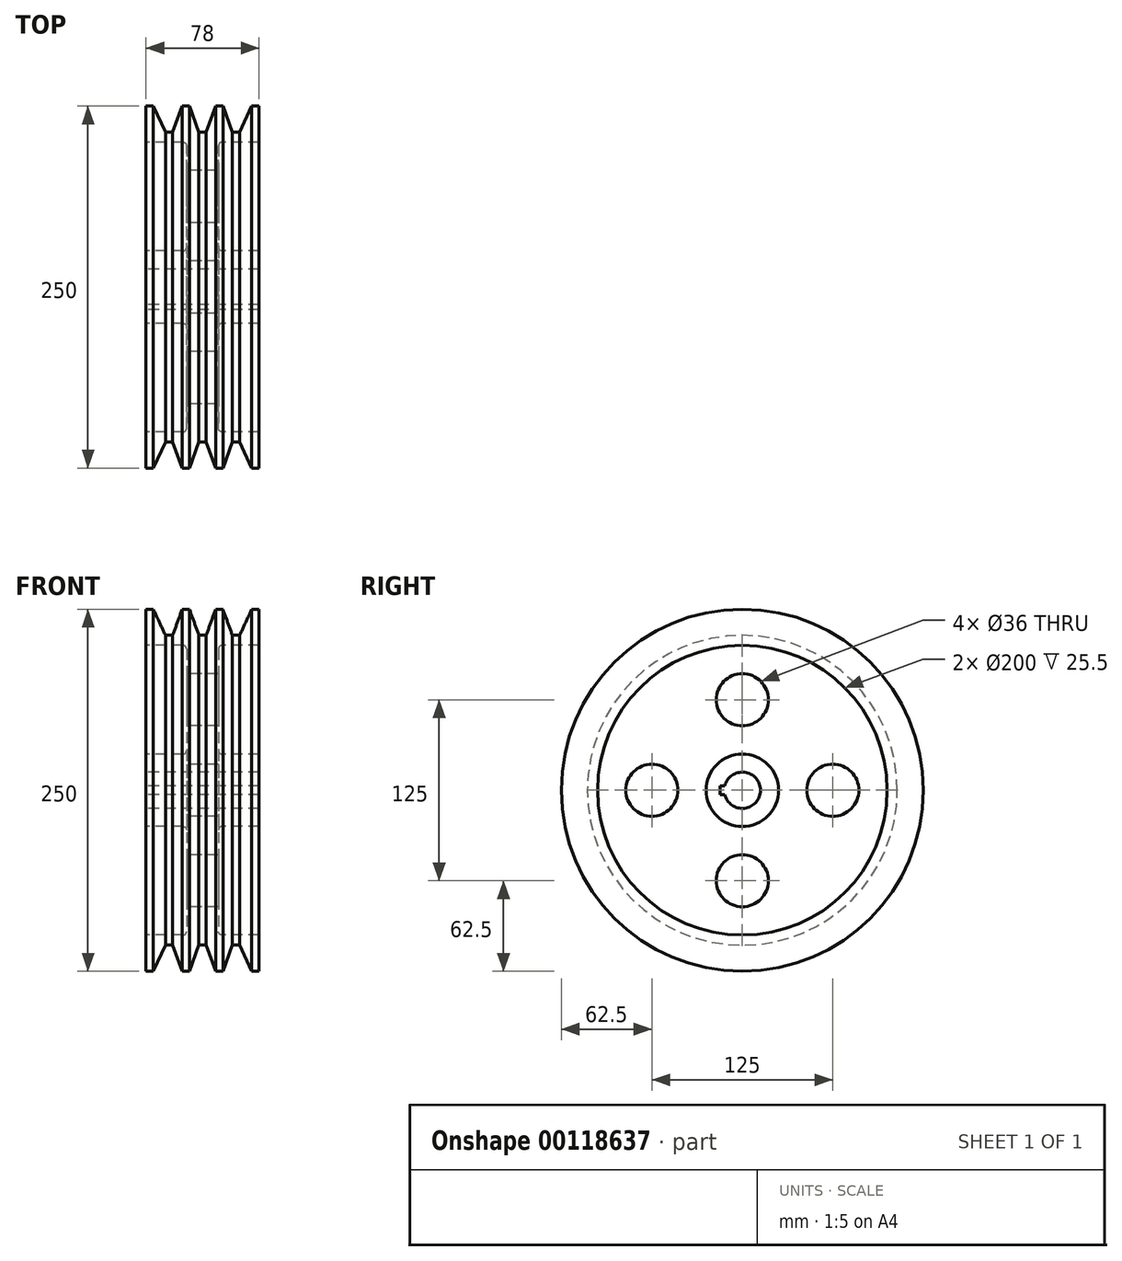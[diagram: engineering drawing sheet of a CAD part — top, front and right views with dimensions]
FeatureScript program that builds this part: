
annotation { "Feature Type Name" : "Feature", "Feature Type Description" : "" }
export const myFeature = defineFeature(function(context is Context, id is Id, definition is map)
    precondition{}
    {
        {
            var Q0;
            Q0=qCreatedBy(makeId("Front.planeOp"),FACE);
            var sketch = newSketch(context, id + "F0", { "sketchPlane" : qUnion([Q0])});
            skLineSegment(sketch, "E0", {"start": v(-39, 0) * mm, "end": v(39, 0) * mm});
            skLineSegment(sketch, "E1.0", {"start": v(-39, 25) * mm, "end": v(-11, 25) * mm});
            skLineSegment(sketch, "E2.0", {"start": v(11, 25) * mm, "end": v(11, 100) * mm});
            skLineSegment(sketch, "E3.0", {"start": v(-11, 25) * mm, "end": v(-11, 100) * mm});
            skLineSegment(sketch, "E4.0", {"start": v(-39, 100) * mm, "end": v(-11, 100) * mm});
            skLineSegment(sketch, "E5", {"start": v(-39, 125) * mm, "end": v(-39, 100) * mm});
            skLineSegment(sketch, "E6", {"start": v(39, 125) * mm, "end": v(39, 100) * mm});
            skLineSegment(sketch, "E7.0", {"start": v(-39, 12.5) * mm, "end": v(39, 12.5) * mm});
            skLineSegment(sketch, "E8.trimOffspring", {"start": v(11, 25) * mm, "end": v(39, 25) * mm});
            skLineSegment(sketch, "E9.trimOffspring", {"start": v(11, 100) * mm, "end": v(39, 100) * mm});
            skLineSegment(sketch, "E10", {"start": v(-39, 25) * mm, "end": v(-39, 12.5) * mm});
            skLineSegment(sketch, "E11", {"start": v(39, 25) * mm, "end": v(39, 12.5) * mm});
            skLineSegment(sketch, "E12", {"start": v(-2.5, 107) * mm, "end": v(2.5, 107) * mm});
            skLineSegment(sketch, "E13", {"start": v(-2.5, 107) * mm, "end": v(-9.05, 125) * mm});
            skLineSegment(sketch, "E14", {"start": v(2.5, 107) * mm, "end": v(9.05, 125) * mm});
            skLineSegment(sketch, "E15", {"start": v(9.05, 125) * mm, "end": v(14.05, 125) * mm});
            skLineSegment(sketch, "E16.MirrorCS", {"start": v(20.6, 107) * mm, "end": v(14.05, 125) * mm});
            skLineSegment(sketch, "E17", {"start": v(20.6, 107) * mm, "end": v(25.6, 107) * mm});
            skLineSegment(sketch, "E18", {"start": v(39, 125) * mm, "end": v(34, 125) * mm});
            skLineSegment(sketch, "E19", {"start": v(34, 125) * mm, "end": v(25.6, 107) * mm});
            skLineSegment(sketch, "E20.MirrorCS", {"start": v(-9.05, 125) * mm, "end": v(-14.05, 125) * mm});
            skLineSegment(sketch, "E21.MirrorCS", {"start": v(-20.6, 107) * mm, "end": v(-14.05, 125) * mm});
            skLineSegment(sketch, "E22", {"start": v(-20.6, 107) * mm, "end": v(-25.6, 107) * mm});
            skLineSegment(sketch, "E23.MirrorCS", {"start": v(-25.6, 107) * mm, "end": v(-34, 125) * mm});
            skLineSegment(sketch, "E24", {"start": v(-39, 125) * mm, "end": v(-34, 125) * mm});
            skSolve(sketch);
        }
        {
            var Q0;
            Q0=makeQuery(id+"F0.imprint","IMPRINT",FACE,{"disambiguationData":[TD([[makeQuery(id+"F0.imprint","IMPRINT",EDGE,{"derivedFrom":sQuery(id+"F0.wireOp",EDGE,"E1.0")}),-1.0]])]});
            var Q1;
            Q1=sQuery(id+"F0.wireOp",EDGE,"E0");
            revolve(context, id + "F1", {"entities" : qUnion([Q0]), "axis" : qUnion([Q1]), "revolveType" : RevolveType.FULL});
        }
        {
            var Q0;
            Q0=makeQuery(id+"F1.opRevolve","SWEPT_FACE",FACE,{"disambiguationData":[OSD([sQuery(id+"F0.wireOp",EDGE,"E3.0")])]});
            var sketch = newSketch(context, id + "F2", { "sketchPlane" : qUnion([Q0])});
            skCircle(sketch, "E25", {"center": v(0, 62.5) * mm, "radius": 18 * mm});
            skCircle(sketch, "E26.1.0", {"center": v(-62.5, 0) * mm, "radius": 18 * mm});
            skCircle(sketch, "E26.2.0", {"center": v(0, -62.5) * mm, "radius": 18 * mm});
            skCircle(sketch, "E26.3.0", {"center": v(62.5, 0) * mm, "radius": 18 * mm});
            skPoint(sketch, "E26.center", {"position": v(0, 0) * mm});
            skSolve(sketch);
        }
        {
            var Q0;
            Q0=makeQuery(id+"F2.imprint","IMPRINT",FACE,{"disambiguationData":[TD([[makeQuery(id+"F2.imprint","IMPRINT",EDGE,{"derivedFrom":sQuery(id+"F2.wireOp",EDGE,"E26.1.0")}),1.0]])]});
            var Q1;
            Q1=makeQuery(id+"F2.imprint","IMPRINT",FACE,{"disambiguationData":[TD([[makeQuery(id+"F2.imprint","IMPRINT",EDGE,{"derivedFrom":sQuery(id+"F2.wireOp",EDGE,"E26.2.0")}),1.0]])]});
            var Q2;
            Q2=makeQuery(id+"F2.imprint","IMPRINT",FACE,{"disambiguationData":[TD([[makeQuery(id+"F2.imprint","IMPRINT",EDGE,{"derivedFrom":sQuery(id+"F2.wireOp",EDGE,"E26.3.0")}),1.0]])]});
            var Q3;
            Q3=makeQuery(id+"F2.imprint","IMPRINT",FACE,{"disambiguationData":[TD([[makeQuery(id+"F2.imprint","IMPRINT",EDGE,{"derivedFrom":sQuery(id+"F2.wireOp",EDGE,"E25")}),1.0]])]});
            extrude(context, id + "F3", {"entities" : qUnion([Q0, Q1, Q2, Q3]), "operationType" : NewBodyOperationType.REMOVE, "endBound" : BoundingType.THROUGH_ALL, "oppositeDirection" : true, "depth" : 25 * mm});
        }
        {
            var Q0;
            Q0=makeQuery(id+"F1.opRevolve","SWEPT_FACE",FACE,{"disambiguationData":[OSD([sQuery(id+"F0.wireOp",EDGE,"E10")])]});
            var sketch = newSketch(context, id + "F4", { "sketchPlane" : qUnion([Q0])});
            skLineSegment(sketch, "E27.bottom", {"start": v(10, 3) * mm, "end": v(15.5, 3) * mm});
            skLineSegment(sketch, "E27.top", {"start": v(10, -3) * mm, "end": v(15.5, -3) * mm});
            skLineSegment(sketch, "E27.left", {"start": v(10, 3) * mm, "end": v(10, -3) * mm});
            skLineSegment(sketch, "E27.right", {"start": v(15.5, 3) * mm, "end": v(15.5, -3) * mm});
            skSolve(sketch);
        }
        {
            var Q0;
            {var subQ0=sQuery(id+"F4.wireOp",EDGE,"E27.right");Q0=makeQuery(id+"F4.imprint","IMPRINT",FACE,{"disambiguationData":[TD([[makeQuery(id+"F4.imprint","IMPRINT",EDGE,{"derivedFrom":subQ0}),-1.0]])]});}
            extrude(context, id + "F5", {"entities" : qUnion([Q0]), "operationType" : NewBodyOperationType.REMOVE, "endBound" : BoundingType.THROUGH_ALL, "oppositeDirection" : true, "depth" : 25 * mm});
        }
        {
            var Q0;
            Q0=makeQuery(id+"F1.opRevolve","SWEPT_EDGE",EDGE,{"disambiguationData":[OSD([sQuery(id+"F0.wireOp",EDGE,"E3.0"),sQuery(id+"F0.wireOp",EDGE,"E4.0")])]});
            var Q1;
            Q1=makeQuery(id+"F1.opRevolve","SWEPT_EDGE",EDGE,{"disambiguationData":[OSD([sQuery(id+"F0.wireOp",EDGE,"E1.0"),sQuery(id+"F0.wireOp",EDGE,"E3.0")])]});
            var Q2;
            Q2=makeQuery(id+"F1.opRevolve","SWEPT_EDGE",EDGE,{"disambiguationData":[OSD([sQuery(id+"F0.wireOp",EDGE,"E2.0"),sQuery(id+"F0.wireOp",EDGE,"E8.trimOffspring")])]});
            var Q3;
            Q3=makeQuery(id+"F1.opRevolve","SWEPT_EDGE",EDGE,{"disambiguationData":[OSD([sQuery(id+"F0.wireOp",EDGE,"E2.0"),sQuery(id+"F0.wireOp",EDGE,"E9.trimOffspring")])]});
            fillet(context, id + "F6", {"entities" : qUnion([Q0, Q1, Q2, Q3]), "radius" : 2.5 * mm, "tangentPropagation" : true, "allowEdgeOverflow" : false});
        }
    });
